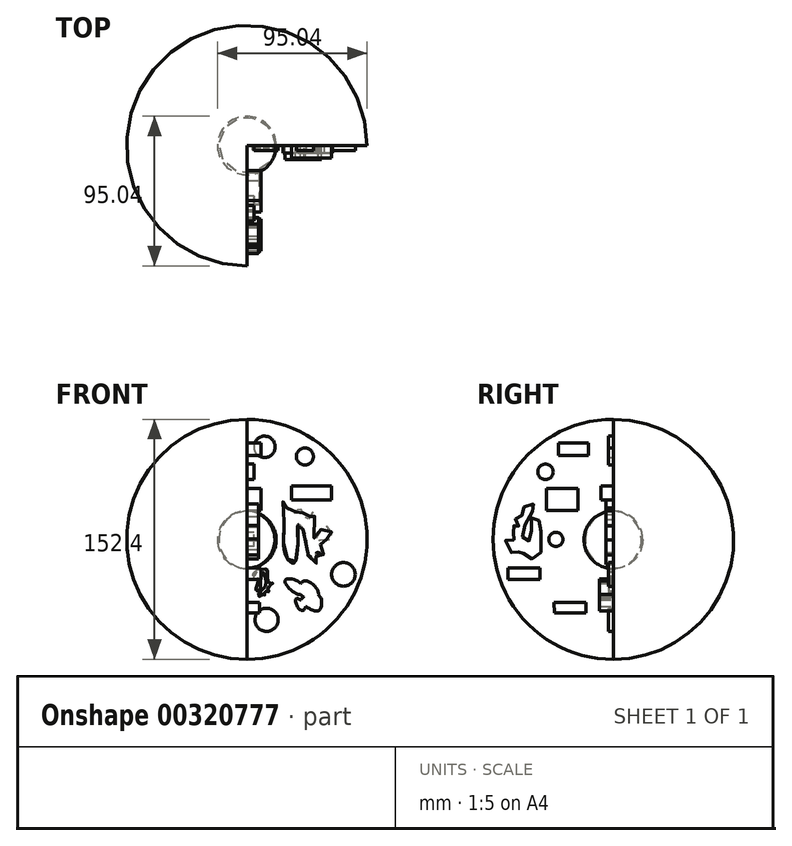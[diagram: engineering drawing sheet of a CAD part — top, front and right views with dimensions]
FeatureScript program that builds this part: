
annotation { "Feature Type Name" : "Feature", "Feature Type Description" : "" }
export const myFeature = defineFeature(function(context is Context, id is Id, definition is map)
    precondition{}
    {
        {
            var Q0;
            Q0=qCreatedBy(makeId("Front.planeOp"),FACE);
            var sketch = newSketch(context, id + "F0", { "sketchPlane" : qUnion([Q0])});
            skLineSegment(sketch, "E0", {"start": v(0, -76.2) * mm, "end": v(0, 76.2) * mm});
            skArc(sketch, "E1", {"start": v(0, -76.2) * mm, "mid": v(76.41, 0) * mm, "end": v(0, 76.2) * mm});
            skSolve(sketch);
        }
        {
            var Q0;
            Q0 = qSketchRegion(id + "F0", true);
            var Q1;
            Q1=sQuery(id+"F0.wireOp",EDGE,"E0");
            revolve(context, id + "F1", {"entities" : qUnion([Q0]), "axis" : qUnion([Q1]), "revolveType" : RevolveType.ONE_DIRECTION, "angle" : 270 * degree});
        }
        {
            var Q0;
            Q0=qCreatedBy(makeId("Front.planeOp"),FACE);
            var sketch = newSketch(context, id + "F2", { "sketchPlane" : qUnion([Q0])});
            skLineSegment(sketch, "E2", {"start": v(0, -18.52) * mm, "end": v(0, 17.89) * mm});
            skArc(sketch, "E3", {"start": v(0, -18.52) * mm, "mid": v(17.79, -0.31) * mm, "end": v(0, 17.89) * mm});
            skSolve(sketch);
        }
        {
            var Q0;
            Q0 = qSketchRegion(id + "F2", true);
            var Q1;
            Q1=sQuery(id+"F2.wireOp",EDGE,"E2");
            revolve(context, id + "F3", {"entities" : qUnion([Q0]), "axis" : qUnion([Q1]), "revolveType" : RevolveType.FULL});
        }
        {
            var Q0;
            Q0=qCreatedBy(makeId("Right.planeOp"),FACE);
            var sketch = newSketch(context, id + "F4", { "sketchPlane" : qUnion([Q0])});
            skLineSegment(sketch, "E4", {"start": v(-37.43, -46.7) * mm, "end": v(-17.43, -46.7) * mm});
            skLineSegment(sketch, "E5", {"start": v(-17.43, -46.7) * mm, "end": v(-17.43, -39.93) * mm});
            skLineSegment(sketch, "E6", {"start": v(-17.43, -39.93) * mm, "end": v(-37.68, -39.93) * mm});
            skLineSegment(sketch, "E7", {"start": v(-37.68, -39.93) * mm, "end": v(-37.43, -46.7) * mm});
            skSolve(sketch);
        }
        {
            var Q0;
            Q0 = qSketchRegion(id + "F4", true);
            extrude(context, id + "F5", {"entities" : qUnion([Q0]), "depth" : 8 * mm});
        }
        {
            var Q0;
            Q0=makeQuery(id+"F0.imprint","IMPRINT",FACE,{"disambiguationData":[TD([[makeQuery(id+"F0.imprint","IMPRINT",EDGE,{"derivedFrom":sQuery(id+"F0.wireOp",EDGE,"E0")}),-1.0]])]});
            var sketch = newSketch(context, id + "F6", { "sketchPlane" : qUnion([Q0])});
            skFitSpline(sketch, "E8", {"points": [v(7.37, -24.61) * mm, v(5.9, -32.26) * mm, v(8.22, -32) * mm, v(8.59, -29.16) * mm, v(10.09, -20.5) * mm, v(11.9, -24.72) * mm, v(11.11, -30.81) * mm, v(7.3, -34.96) * mm, v(8.35, -36.6) * mm, v(9.23, -34.5) * mm, v(11.49, -35.63) * mm, v(11.1, -33.27) * mm, v(14, -33.37) * mm, v(13.25, -31.26) * mm, v(16.62, -27.74) * mm, v(13.81, -27.7) * mm, v(13.16, -19.76) * mm, v(10.22, -18.9) * mm, v(4.8, -20.73) * mm, v(3.78, -23.3) * mm, v(6.35, -20.67) * mm, v(3.91, -25.45) * mm, v(7.37, -24.61) * mm]});
            skSolve(sketch);
        }
        {
            var Q0;
            Q0 = qSketchRegion(id + "F6", true);
            extrude(context, id + "F7", {"entities" : qUnion([Q0]), "depth" : 2.76 * mm});
        }
        {
            var Q0;
            Q0=qCreatedBy(makeId("Front.planeOp"),FACE);
            var sketch = newSketch(context, id + "F8", { "sketchPlane" : qUnion([Q0])});
            skFitSpline(sketch, "E9", {"points": [v(23.65, 11.04) * mm, v(24.5, -9.58) * mm, v(29.71, -15.16) * mm, v(32.41, 0) * mm, v(33.06, 9.58) * mm, v(37.87, 0) * mm, v(38.12, -9.83) * mm, v(41.75, -11.8) * mm, v(44.7, -15.92) * mm, v(44.33, -8.52) * mm, v(49.4, -9.8) * mm, v(46.16, 0) * mm, v(54.05, 0) * mm, v(49.9, 8.44) * mm, v(43.07, 0) * mm, v(42.58, 17.86) * mm, v(38.32, 12.55) * mm, v(33.64, 19.78) * mm, v(28.94, 15.89) * mm, v(23.32, 24.77) * mm, v(23.65, 11.04) * mm]});
            skSolve(sketch);
        }
        {
            var Q0;
            Q0 = qSketchRegion(id + "F8", true);
            extrude(context, id + "F9", {"entities" : qUnion([Q0]), "depth" : 4.78 * mm});
        }
        {
            var Q0;
            Q0 = qSketchRegion(id + "F0", true);
            var sketch = newSketch(context, id + "F10", { "sketchPlane" : qUnion([Q0])});
            skFitSpline(sketch, "E10", {"points": [v(31.33, -37.71) * mm, v(34.22, -45) * mm, v(37.21, -42.47) * mm, v(31.33, -37.71) * mm]});
            skFitSpline(sketch, "E11", {"points": [v(37.21, -42.47) * mm, v(46.05, -45) * mm, v(45.3, -35.15) * mm, v(34.22, -38.52) * mm, v(37.21, -42.47) * mm]});
            skFitSpline(sketch, "E12", {"points": [v(45.3, -35.15) * mm, v(36.73, -26.37) * mm, v(34.22, -35.15) * mm, v(45.3, -35.15) * mm]});
            skFitSpline(sketch, "E13", {"points": [v(34.22, -35.15) * mm, v(34.22, -28.07) * mm, v(24.22, -26.37) * mm, v(34.22, -35.15) * mm]});
            skSolve(sketch);
        }
        {
            var Q0;
            Q0 = qSketchRegion(id + "F10", true);
            extrude(context, id + "F11", {"entities" : qUnion([Q0]), "depth" : 8.97 * mm});
        }
        {
            var Q0;
            Q0=qCreatedBy(makeId("Front.planeOp"),FACE);
            var sketch = newSketch(context, id + "F12", { "sketchPlane" : qUnion([Q0])});
            skCircle(sketch, "E14", {"center": v(12.55, -51.1) * mm, "radius": 7.36 * mm});
            skCircle(sketch, "E15", {"center": v(36.89, 52.6) * mm, "radius": 5.4 * mm});
            skCircle(sketch, "E16", {"center": v(11.25, 58.75) * mm, "radius": 6.8 * mm});
            skCircle(sketch, "E17", {"center": v(61.36, -22.26) * mm, "radius": 7.52 * mm});
            skSolve(sketch);
        }
        {
            var Q0;
            Q0 = qSketchRegion(id + "F12", true);
            extrude(context, id + "F13", {"entities" : qUnion([Q0]), "depth" : 3.18 * mm});
        }
        {
            var Q0;
            Q0=qCreatedBy(makeId("Right.planeOp"),FACE);
            var sketch = newSketch(context, id + "F14", { "sketchPlane" : qUnion([Q0])});
            skCircle(sketch, "E18", {"center": v(-36.56, 0) * mm, "radius": 4.5 * mm});
            skCircle(sketch, "E19", {"center": v(-43.13, 42.88) * mm, "radius": 4.92 * mm});
            skSolve(sketch);
        }
        {
            var Q0;
            Q0 = qSketchRegion(id + "F14", true);
            extrude(context, id + "F15", {"entities" : qUnion([Q0]), "depth" : 4.47 * mm});
        }
        {
            var Q0;
            Q0=qCreatedBy(makeId("Right.planeOp"),FACE);
            var sketch = newSketch(context, id + "F16", { "sketchPlane" : qUnion([Q0])});
            skLineSegment(sketch, "E20.bottom", {"start": v(-22.54, 32.2) * mm, "end": v(-42.36, 32.2) * mm});
            skLineSegment(sketch, "E20.top", {"start": v(-22.54, 18.45) * mm, "end": v(-42.36, 18.45) * mm});
            skLineSegment(sketch, "E20.left", {"start": v(-22.54, 32.2) * mm, "end": v(-22.54, 18.45) * mm});
            skLineSegment(sketch, "E20.right", {"start": v(-42.36, 32.2) * mm, "end": v(-42.36, 18.45) * mm});
            skLineSegment(sketch, "E21.bottom", {"start": v(-46.52, -25.48) * mm, "end": v(-66.91, -25.48) * mm});
            skLineSegment(sketch, "E21.top", {"start": v(-46.52, -18.3) * mm, "end": v(-66.91, -18.3) * mm});
            skLineSegment(sketch, "E21.left", {"start": v(-46.52, -25.48) * mm, "end": v(-46.52, -18.3) * mm});
            skLineSegment(sketch, "E21.right", {"start": v(-66.91, -25.48) * mm, "end": v(-66.91, -18.3) * mm});
            skLineSegment(sketch, "E22.bottom", {"start": v(-15.95, 53.42) * mm, "end": v(-34.83, 53.42) * mm});
            skLineSegment(sketch, "E22.top", {"start": v(-15.95, 61.11) * mm, "end": v(-34.83, 61.11) * mm});
            skLineSegment(sketch, "E22.left", {"start": v(-15.95, 53.42) * mm, "end": v(-15.95, 61.11) * mm});
            skLineSegment(sketch, "E22.right", {"start": v(-34.83, 53.42) * mm, "end": v(-34.83, 61.11) * mm});
            skSolve(sketch);
        }
        {
            var Q0;
            Q0 = qSketchRegion(id + "F16", true);
            extrude(context, id + "F17", {"entities" : qUnion([Q0]), "depth" : 9 * mm});
        }
        {
            var Q0;
            Q0=makeQuery(id+"F0.imprint","IMPRINT",FACE,{"disambiguationData":[TD([[makeQuery(id+"F0.imprint","IMPRINT",EDGE,{"derivedFrom":sQuery(id+"F0.wireOp",EDGE,"E0")}),-1.0]])]});
            var sketch = newSketch(context, id + "F18", { "sketchPlane" : qUnion([Q0])});
            skLineSegment(sketch, "E23.bottom", {"start": v(53.67, 25) * mm, "end": v(28.26, 25) * mm});
            skLineSegment(sketch, "E23.top", {"start": v(53.67, 33.98) * mm, "end": v(28.26, 33.98) * mm});
            skLineSegment(sketch, "E23.left", {"start": v(53.67, 25) * mm, "end": v(53.67, 33.98) * mm});
            skLineSegment(sketch, "E23.right", {"start": v(28.26, 25) * mm, "end": v(28.26, 33.98) * mm});
            skSolve(sketch);
        }
        {
            var Q0;
            Q0 = qSketchRegion(id + "F18", true);
            extrude(context, id + "F19", {"entities" : qUnion([Q0]), "depth" : 7.9 * mm});
        }
        {
            var Q0;
            Q0=qCreatedBy(makeId("Right.planeOp"),FACE);
            var sketch = newSketch(context, id + "F20", { "sketchPlane" : qUnion([Q0])});
            skFitSpline(sketch, "E24", {"points": [v(-46.12, -8.33) * mm, v(-46.22, 0) * mm, v(-46.88, 11.33) * mm, v(-52.05, 13.65) * mm, v(-52.26, 0) * mm, v(-56.98, 0) * mm, v(-54.64, 11.93) * mm, v(-50.26, 22.07) * mm, v(-56.92, 20.2) * mm, v(-58.5, 14.42) * mm, v(-62.72, 12.29) * mm, v(-59.83, 7.62) * mm, v(-64.6, 8.59) * mm, v(-62.01, 0) * mm, v(-68.22, 0) * mm, v(-62.58, -9.88) * mm, v(-59.22, -6.9) * mm, v(-53.84, -12.02) * mm, v(-46.12, -8.33) * mm]});
            skSolve(sketch);
        }
        {
            var Q0;
            Q0 = qSketchRegion(id + "F20", true);
            extrude(context, id + "F21", {"entities" : qUnion([Q0]), "depth" : 7.33 * mm});
        }
    });
